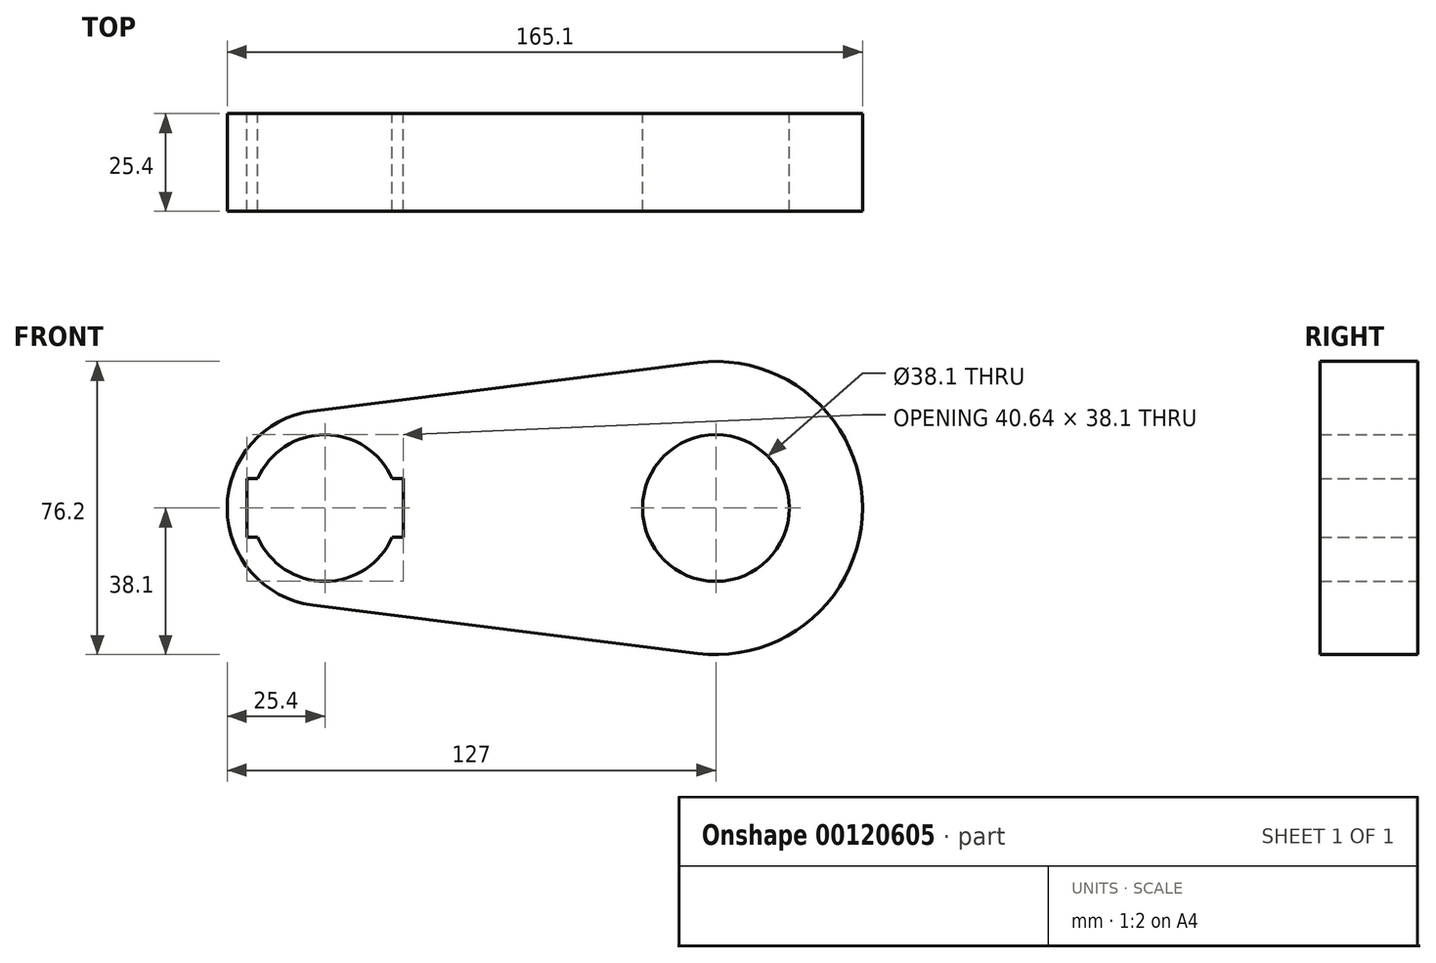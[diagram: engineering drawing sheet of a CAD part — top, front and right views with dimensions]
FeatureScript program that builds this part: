
annotation { "Feature Type Name" : "Feature", "Feature Type Description" : "" }
export const myFeature = defineFeature(function(context is Context, id is Id, definition is map)
    precondition{}
    {
        {
            var Q0;
            Q0=qCreatedBy(makeId("Front.planeOp"),FACE);
            var sketch = newSketch(context, id + "F0", { "sketchPlane" : qUnion([Q0])});
            skCircle(sketch, "E0", {"center": v(0, 0) * mm, "radius": 38.1 * mm});
            skCircle(sketch, "E1", {"center": v(-101.6, 0) * mm, "radius": 25.4 * mm});
            skLineSegment(sketch, "E2", {"start": v(-4.76, 37.8) * mm, "end": v(-104.78, 25.2) * mm});
            skLineSegment(sketch, "E3", {"start": v(-4.76, -37.8) * mm, "end": v(-104.78, -25.2) * mm});
            skCircle(sketch, "E4", {"center": v(-101.6, 0) * mm, "radius": 19.05 * mm});
            skCircle(sketch, "E5", {"center": v(0, 0) * mm, "radius": 19.05 * mm});
            skLineSegment(sketch, "E6.bottom", {"start": v(-81.28, 7.62) * mm, "end": v(-121.92, 7.62) * mm});
            skLineSegment(sketch, "E6.top", {"start": v(-81.28, -7.62) * mm, "end": v(-121.92, -7.62) * mm});
            skLineSegment(sketch, "E6.left", {"start": v(-81.28, 7.62) * mm, "end": v(-81.28, -7.62) * mm});
            skLineSegment(sketch, "E6.right", {"start": v(-121.92, 7.62) * mm, "end": v(-121.92, -7.62) * mm});
            skSolve(sketch);
        }
        {
            var Q0;
            Q0=makeQuery(id+"F0.imprint","IMPRINT",FACE,{"disambiguationData":[TD([[makeQuery(id+"F0.imprint","IMPRINT",EDGE,{"derivedFrom":sQuery(id+"F0.wireOp",EDGE,"E5")}),-1.0]])]});
            var Q1;
            {var subQ0=sQuery(id+"F0.wireOp",EDGE,"E2");Q1=makeQuery(id+"F0.imprint","IMPRINT",FACE,{"disambiguationData":[TD([[makeQuery(id+"F0.imprint","IMPRINT",EDGE,{"derivedFrom":subQ0}),1.0]])]});}
            var Q2;
            {var subQ8=sQuery(id+"F0.wireOp",EDGE,"E6.left");Q2=makeQuery(id+"F0.imprint","IMPRINT",FACE,{"disambiguationData":[TD([[makeQuery(id+"F0.imprint","IMPRINT",EDGE,{"derivedFrom":subQ8}),1.0]])]});}
            extrude(context, id + "F1", {"entities" : qUnion([Q0, Q1, Q2]), "depth" : 25.4 * mm});
        }
    });
